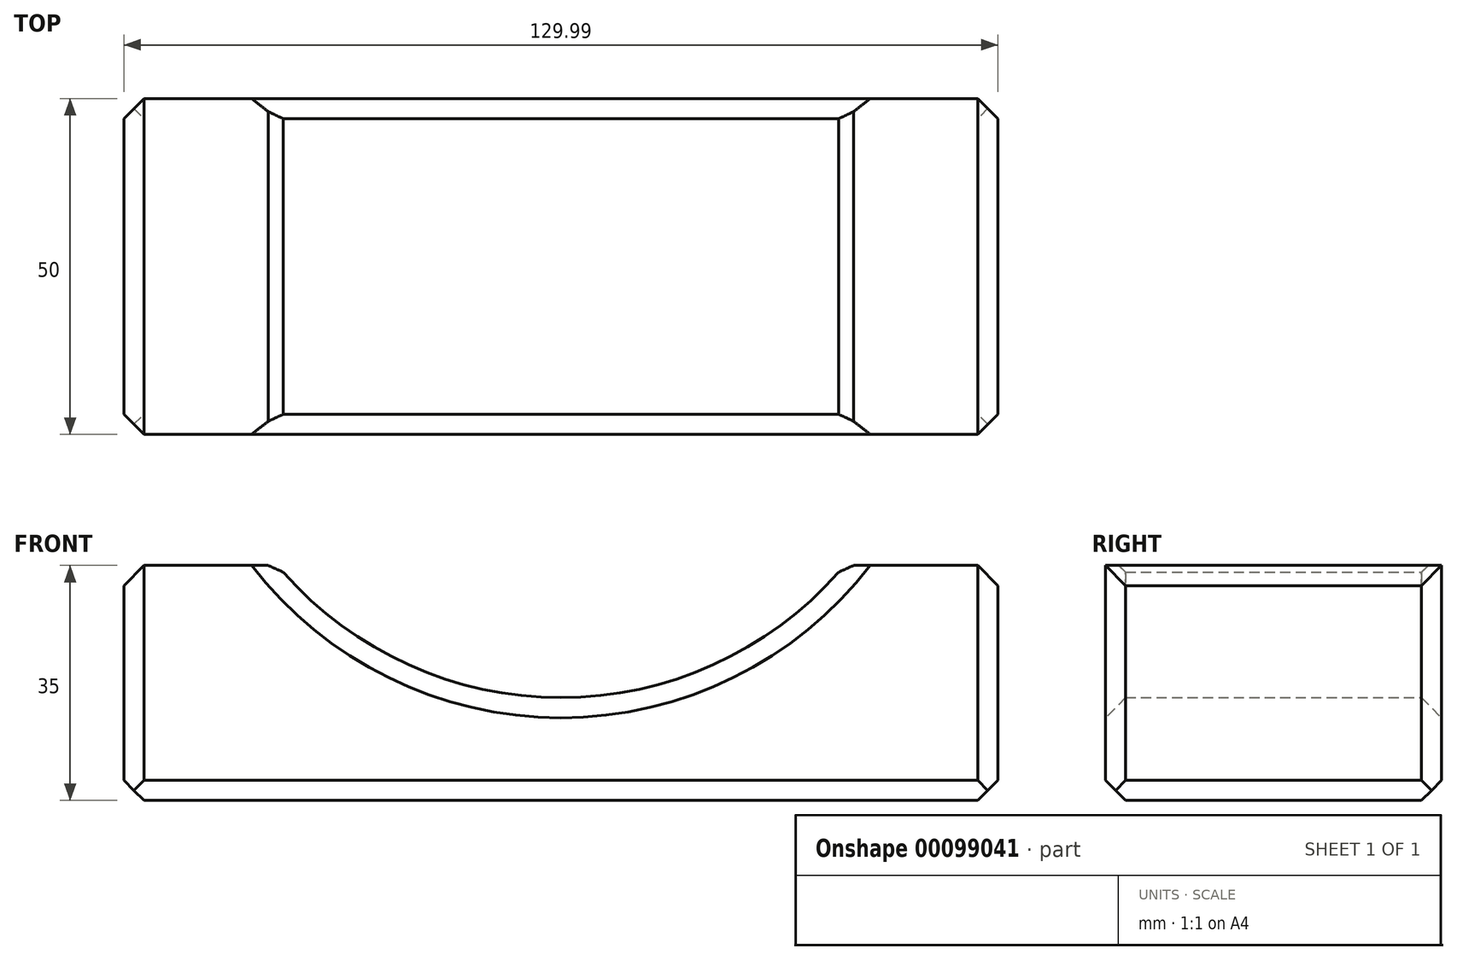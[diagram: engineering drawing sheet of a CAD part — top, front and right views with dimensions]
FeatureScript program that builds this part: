
annotation { "Feature Type Name" : "Feature", "Feature Type Description" : "" }
export const myFeature = defineFeature(function(context is Context, id is Id, definition is map)
    precondition{}
    {
        {
            var Q0;
            Q0=qCreatedBy(makeId("Front.planeOp"),FACE);
            var sketch = newSketch(context, id + "F0", { "sketchPlane" : qUnion([Q0])});
            skLineSegment(sketch, "E0.top", {"start": v(-62.88, -36.12) * mm, "end": v(67.11, -36.12) * mm});
            skLineSegment(sketch, "E0.left", {"start": v(-62.88, -1.12) * mm, "end": v(-62.88, -36.12) * mm});
            skLineSegment(sketch, "E0.right", {"start": v(67.11, -1.12) * mm, "end": v(67.11, -36.12) * mm});
            skArc(sketch, "E1", {"start": v(-40.05, -1.12) * mm, "mid": v(2.11, -20.81) * mm, "end": v(44.28, -1.12) * mm});
            skLineSegment(sketch, "E2", {"start": v(-62.88, -1.12) * mm, "end": v(-40.05, -1.12) * mm});
            skPoint(sketch, "E3.orphan", {"position": v(-52.88, 33.88) * mm});
            skPoint(sketch, "E4.orphan", {"position": v(57.11, 33.88) * mm});
            skLineSegment(sketch, "E5.trimOffspring", {"start": v(44.28, -1.12) * mm, "end": v(67.11, -1.12) * mm});
            skPoint(sketch, "E6.orphan", {"position": v(67.11, 33.88) * mm});
            skPoint(sketch, "E7.orphan", {"position": v(-62.88, 33.88) * mm});
            skSolve(sketch);
        }
        {
            var Q0;
            Q0=makeQuery(id+"F0.imprint","IMPRINT",FACE,{"disambiguationData":[TD([[makeQuery(id+"F0.imprint","IMPRINT",EDGE,{"derivedFrom":sQuery(id+"F0.wireOp",EDGE,"E0.top")}),1.0]])]});
            extrude(context, id + "F1", {"entities" : qUnion([Q0]), "depth" : 50 * mm});
        }
        {
            var Q0;
            Q0=makeQuery(id+"F1.opExtrude","SWEPT_FACE",FACE,{"disambiguationData":[OSD([sQuery(id+"F0.wireOp",EDGE,"E1")])]});
            chamfer(context, id + "F2", {"entities" : qUnion([Q0]), "width" : 3 * mm, "tangentPropagation" : true});
        }
        {
            var Q0;
            Q0=makeQuery(id+"F1.opExtrude","SWEPT_FACE",FACE,{"disambiguationData":[OSD([sQuery(id+"F0.wireOp",EDGE,"E0.right")])]});
            chamfer(context, id + "F3", {"entities" : qUnion([Q0]), "width" : 3 * mm, "tangentPropagation" : true});
        }
        {
            var Q0;
            Q0=makeQuery(id+"F1.opExtrude","SWEPT_FACE",FACE,{"disambiguationData":[OSD([sQuery(id+"F0.wireOp",EDGE,"E0.left")])]});
            chamfer(context, id + "F4", {"entities" : qUnion([Q0]), "width" : 3 * mm, "tangentPropagation" : true});
        }
        {
            var Q0;
            Q0=makeQuery(id+"F1.opExtrude","CAP_EDGE",EDGE,{"disambiguationData":[OSD([sQuery(id+"F0.wireOp",EDGE,"E0.top")])],"isStart":false});
            var Q1;
            Q1=makeQuery(id+"F1.opExtrude","CAP_EDGE",EDGE,{"disambiguationData":[OSD([sQuery(id+"F0.wireOp",EDGE,"E0.top")])],"isStart":true});
            chamfer(context, id + "F5", {"entities" : qUnion([Q0, Q1]), "width" : 3 * mm, "tangentPropagation" : true});
        }
    });
